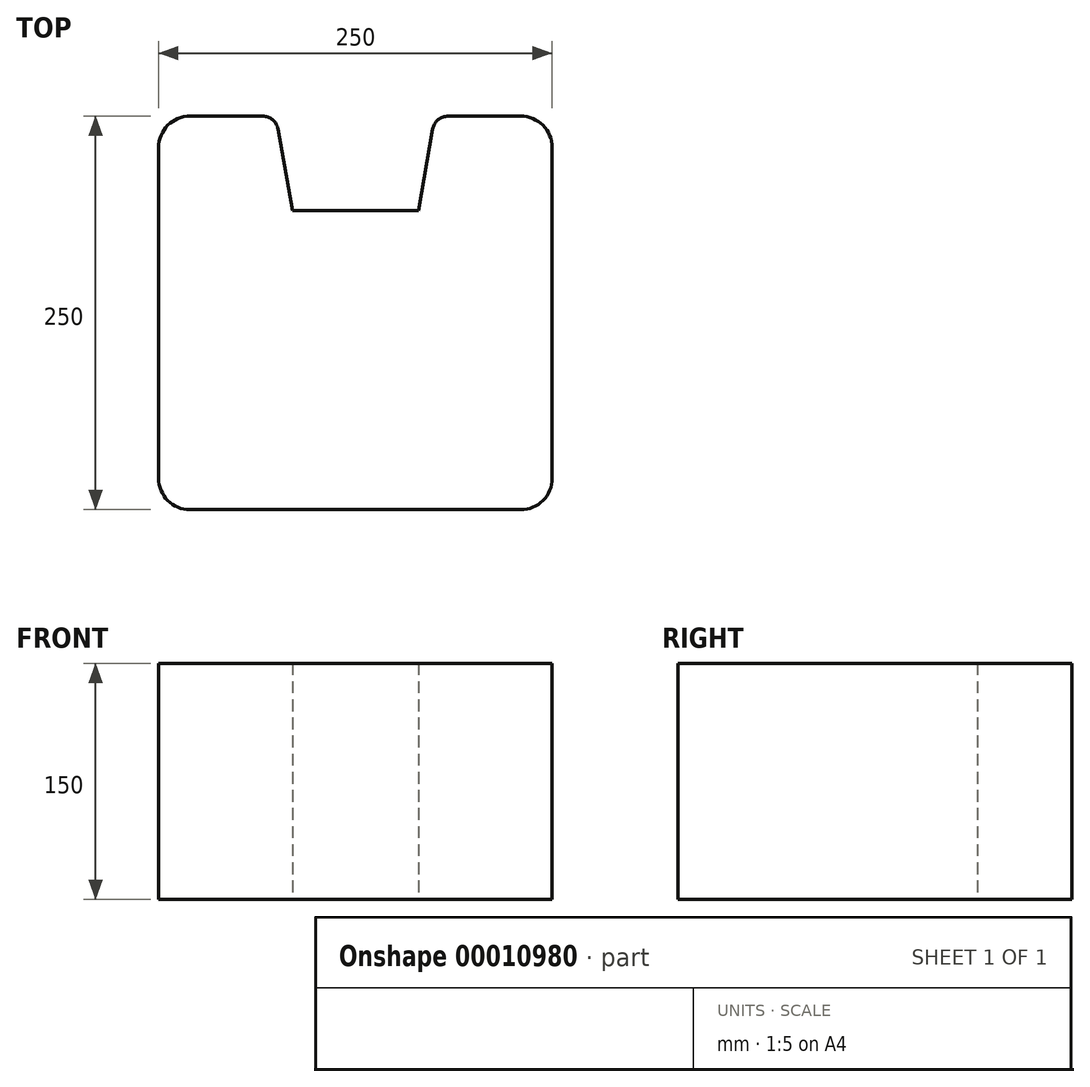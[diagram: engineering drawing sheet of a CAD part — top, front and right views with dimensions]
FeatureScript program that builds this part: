
annotation { "Feature Type Name" : "Feature", "Feature Type Description" : "" }
export const myFeature = defineFeature(function(context is Context, id is Id, definition is map)
    precondition{}
    {
        {
            var Q0;
            Q0=qCreatedBy(makeId("Top.planeOp"),FACE);
            var sketch = newSketch(context, id + "F0", { "sketchPlane" : qUnion([Q0])});
            skLineSegment(sketch, "E0.rect.top", {"start": v(105, -125) * mm, "end": v(-105, -125) * mm});
            skLineSegment(sketch, "E0.rect.left", {"start": v(125, 105) * mm, "end": v(125, -105) * mm});
            skLineSegment(sketch, "E0.rect.right", {"start": v(-125, 105) * mm, "end": v(-125, -105) * mm});
            skPoint(sketch, "E0.rect.middle", {"position": v(0, 0) * mm});
            skLineSegment(sketch, "E1", {"start": v(-105, 125) * mm, "end": v(-58.97, 125) * mm});
            skLineSegment(sketch, "E2", {"start": v(105, 125) * mm, "end": v(58.97, 125) * mm});
            skLineSegment(sketch, "E3", {"start": v(-49.12, 116.74) * mm, "end": v(-40, 65) * mm});
            skLineSegment(sketch, "E4", {"start": v(-40, 65) * mm, "end": v(40, 65) * mm});
            skLineSegment(sketch, "E5", {"start": v(40, 65) * mm, "end": v(49.12, 116.74) * mm});
            skPoint(sketch, "E6.visualSharp", {"position": v(-125, 125) * mm});
            skArc(sketch, "E6.filletArc", {"start": v(-105, 125) * mm, "mid": v(-119.14, 119.14) * mm, "end": v(-125, 105) * mm});
            skPoint(sketch, "E7.visualSharp", {"position": v(125, 125) * mm});
            skArc(sketch, "E7.filletArc", {"start": v(125, 105) * mm, "mid": v(119.14, 119.14) * mm, "end": v(105, 125) * mm});
            skPoint(sketch, "E8.visualSharp", {"position": v(125, -125) * mm});
            skArc(sketch, "E8.filletArc", {"start": v(105, -125) * mm, "mid": v(119.14, -119.14) * mm, "end": v(125, -105) * mm});
            skPoint(sketch, "E9.visualSharp", {"position": v(-125, -125) * mm});
            skArc(sketch, "E9.filletArc", {"start": v(-125, -105) * mm, "mid": v(-119.14, -119.14) * mm, "end": v(-105, -125) * mm});
            skPoint(sketch, "E10.visualSharp", {"position": v(-50.58, 125) * mm});
            skArc(sketch, "E10.filletArc", {"start": v(-49.12, 116.74) * mm, "mid": v(-52.54, 122.66) * mm, "end": v(-58.97, 125) * mm});
            skPoint(sketch, "E11.visualSharp", {"position": v(50.58, 125) * mm});
            skArc(sketch, "E11.filletArc", {"start": v(58.97, 125) * mm, "mid": v(52.54, 122.66) * mm, "end": v(49.12, 116.74) * mm});
            skPoint(sketch, "E12", {"position": v(0, 65) * mm});
            skSolve(sketch);
        }
        {
            var Q0;
            Q0=makeQuery(id+"F0.imprint","IMPRINT",FACE,{"disambiguationData":[TD([[makeQuery(id+"F0.imprint","IMPRINT",EDGE,{"derivedFrom":sQuery(id+"F0.wireOp",EDGE,"E0.rect.top")}),-1.0]])]});
            extrude(context, id + "F1", {"entities" : qUnion([Q0]), "depth" : 150 * mm});
        }
    });
